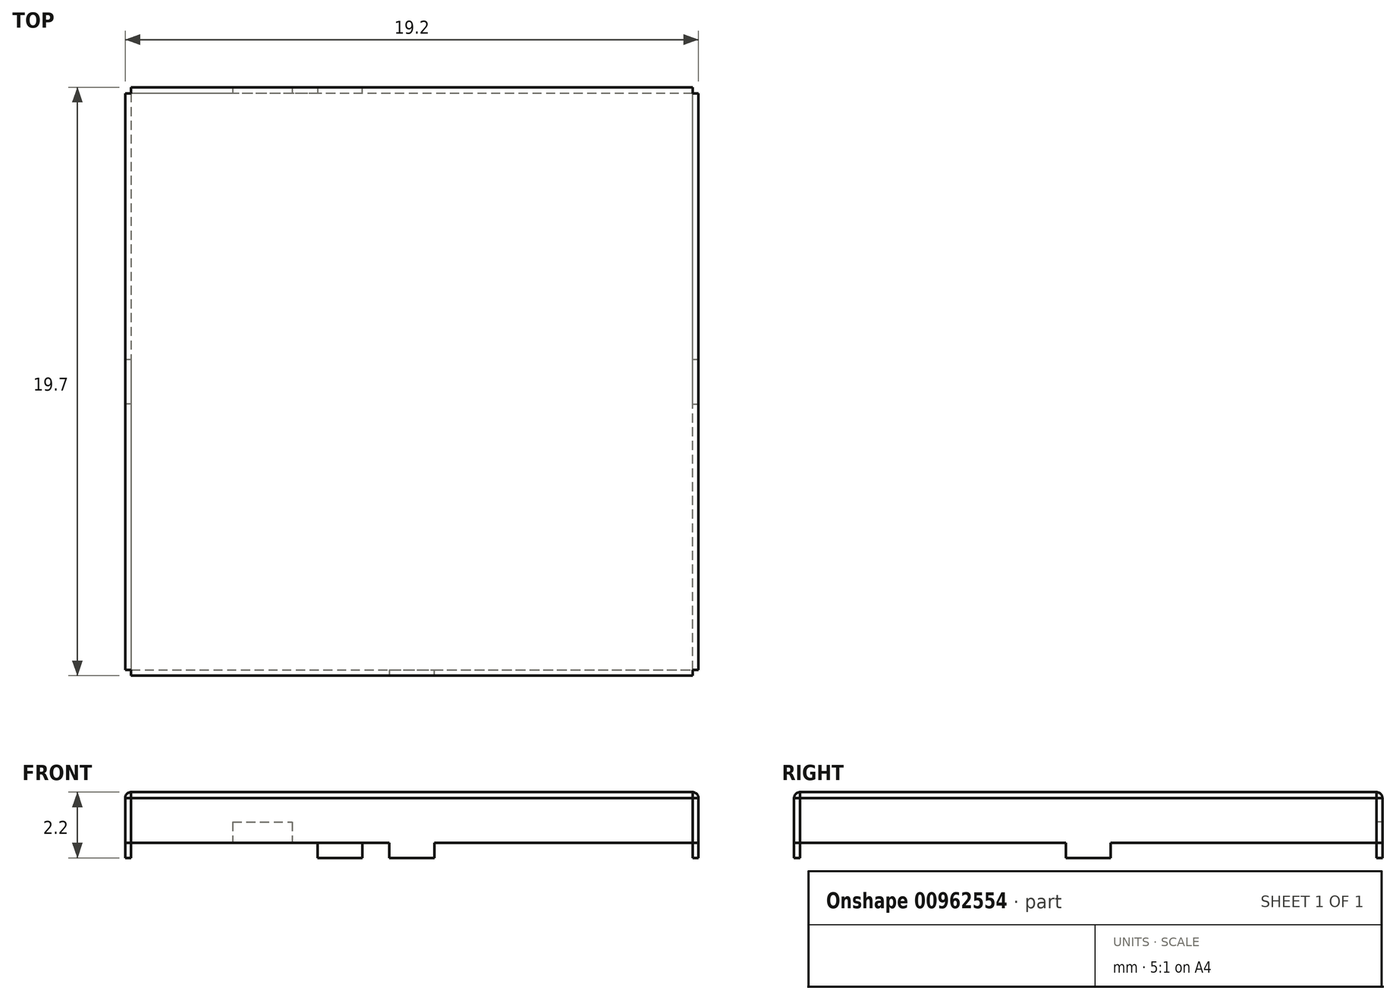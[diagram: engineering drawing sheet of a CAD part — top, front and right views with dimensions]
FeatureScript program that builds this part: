
annotation { "Feature Type Name" : "Feature", "Feature Type Description" : "" }
export const myFeature = defineFeature(function(context is Context, id is Id, definition is map)
    precondition{}
    {
        {
            var Q0;
            Q0=qCreatedBy(makeId("Top.planeOp"),FACE);
            var sketch = newSketch(context, id + "F0", { "sketchPlane" : qUnion([Q0])});
            skLineSegment(sketch, "E0", {"start": v(9.6, 9.65) * mm, "end": v(9.4, 9.65) * mm});
            skLineSegment(sketch, "E1", {"start": v(9.4, 9.65) * mm, "end": v(9.4, 9.85) * mm});
            skLineSegment(sketch, "E2", {"start": v(-9.6, 9.65) * mm, "end": v(-9.4, 9.65) * mm});
            skLineSegment(sketch, "E3", {"start": v(-9.4, 9.65) * mm, "end": v(-9.4, 9.85) * mm});
            skLineSegment(sketch, "E4", {"start": v(9.6, -9.65) * mm, "end": v(9.4, -9.65) * mm});
            skLineSegment(sketch, "E5", {"start": v(9.4, -9.65) * mm, "end": v(9.4, -9.85) * mm});
            skLineSegment(sketch, "E6", {"start": v(-9.6, -9.65) * mm, "end": v(-9.4, -9.65) * mm});
            skLineSegment(sketch, "E7", {"start": v(-9.4, -9.65) * mm, "end": v(-9.4, -9.85) * mm});
            skLineSegment(sketch, "E8", {"start": v(-9.4, 9.85) * mm, "end": v(9.4, 9.85) * mm});
            skLineSegment(sketch, "E9", {"start": v(9.6, 9.65) * mm, "end": v(9.6, -9.65) * mm});
            skLineSegment(sketch, "E10", {"start": v(-9.6, -9.65) * mm, "end": v(-9.6, 9.65) * mm});
            skLineSegment(sketch, "E11", {"start": v(9.4, -9.85) * mm, "end": v(-9.4, -9.85) * mm});
            skLineSegment(sketch, "E12", {"start": v(-9.4, 9.65) * mm, "end": v(-9.4, -9.65) * mm});
            skLineSegment(sketch, "E13", {"start": v(-9.4, -9.65) * mm, "end": v(9.4, -9.65) * mm});
            skLineSegment(sketch, "E14", {"start": v(9.4, -9.65) * mm, "end": v(9.4, 9.65) * mm});
            skLineSegment(sketch, "E15", {"start": v(9.4, 9.65) * mm, "end": v(-9.4, 9.65) * mm});
            skLineSegment(sketch, "E16", {"start": v(-3.15, 9.85) * mm, "end": v(-3.15, 9.65) * mm});
            skLineSegment(sketch, "E17", {"start": v(-1.65, 9.65) * mm, "end": v(-1.65, 9.85) * mm});
            skLineSegment(sketch, "E18", {"start": v(-0.75, -9.65) * mm, "end": v(-0.75, -9.85) * mm});
            skLineSegment(sketch, "E19", {"start": v(0.75, -9.85) * mm, "end": v(0.75, -9.65) * mm});
            skLineSegment(sketch, "E20", {"start": v(-9.6, 0.75) * mm, "end": v(-9.4, 0.75) * mm});
            skLineSegment(sketch, "E21", {"start": v(-9.4, -0.75) * mm, "end": v(-9.6, -0.75) * mm});
            skLineSegment(sketch, "E22", {"start": v(9.4, -0.75) * mm, "end": v(9.6, -0.75) * mm});
            skLineSegment(sketch, "E23", {"start": v(9.4, 0.75) * mm, "end": v(9.6, 0.75) * mm});
            skLineSegment(sketch, "E24", {"start": v(-6, 9.85) * mm, "end": v(-6, 9.65) * mm});
            skLineSegment(sketch, "E25", {"start": v(-4, 9.85) * mm, "end": v(-4, 9.65) * mm});
            skSolve(sketch);
        }
        {
            var Q0;
            {var subQ0=sQuery(id+"F0.wireOp",EDGE,"E3");Q0=makeQuery(id+"F0.imprint","IMPRINT",FACE,{"disambiguationData":[TD([[makeQuery(id+"F0.imprint","IMPRINT",EDGE,{"derivedFrom":subQ0}),-1.0]])]});}
            var Q1;
            {var subQ0=sQuery(id+"F0.wireOp",EDGE,"E24");Q1=makeQuery(id+"F0.imprint","IMPRINT",FACE,{"disambiguationData":[TD([[makeQuery(id+"F0.imprint","IMPRINT",EDGE,{"derivedFrom":subQ0}),1.0]])]});}
            var Q2;
            {var subQ0=sQuery(id+"F0.wireOp",EDGE,"E16");Q2=makeQuery(id+"F0.imprint","IMPRINT",FACE,{"disambiguationData":[TD([[makeQuery(id+"F0.imprint","IMPRINT",EDGE,{"derivedFrom":subQ0}),-1.0]])]});}
            var Q3;
            {var subQ0=sQuery(id+"F0.wireOp",EDGE,"E16");Q3=makeQuery(id+"F0.imprint","IMPRINT",FACE,{"disambiguationData":[TD([[makeQuery(id+"F0.imprint","IMPRINT",EDGE,{"derivedFrom":subQ0}),1.0]])]});}
            var Q4;
            {var subQ0=sQuery(id+"F0.wireOp",EDGE,"E1");Q4=makeQuery(id+"F0.imprint","IMPRINT",FACE,{"disambiguationData":[TD([[makeQuery(id+"F0.imprint","IMPRINT",EDGE,{"derivedFrom":subQ0}),1.0]])]});}
            extrude(context, id + "F1", {"entities" : qUnion([Q0, Q1, Q2, Q3, Q4]), "depth" : 1.5 * mm, "offsetDistance" : 25 * mm});
        }
        {
            var Q0;
            {var subQ0=sQuery(id+"F0.wireOp",EDGE,"E0");Q0=makeQuery(id+"F0.imprint","IMPRINT",FACE,{"disambiguationData":[TD([[makeQuery(id+"F0.imprint","IMPRINT",EDGE,{"derivedFrom":subQ0}),1.0]])]});}
            var Q1;
            {var subQ0=sQuery(id+"F0.wireOp",EDGE,"E22");Q1=makeQuery(id+"F0.imprint","IMPRINT",FACE,{"disambiguationData":[TD([[makeQuery(id+"F0.imprint","IMPRINT",EDGE,{"derivedFrom":subQ0}),1.0]])]});}
            var Q2;
            {var subQ0=sQuery(id+"F0.wireOp",EDGE,"E4");Q2=makeQuery(id+"F0.imprint","IMPRINT",FACE,{"disambiguationData":[TD([[makeQuery(id+"F0.imprint","IMPRINT",EDGE,{"derivedFrom":subQ0}),-1.0]])]});}
            extrude(context, id + "F2", {"entities" : qUnion([Q0, Q1, Q2]), "depth" : 1.5 * mm, "offsetDistance" : 25 * mm});
        }
        {
            var Q0;
            {var subQ0=sQuery(id+"F0.wireOp",EDGE,"E2");Q0=makeQuery(id+"F0.imprint","IMPRINT",FACE,{"disambiguationData":[TD([[makeQuery(id+"F0.imprint","IMPRINT",EDGE,{"derivedFrom":subQ0}),-1.0]])]});}
            var Q1;
            {var subQ0=sQuery(id+"F0.wireOp",EDGE,"E20");Q1=makeQuery(id+"F0.imprint","IMPRINT",FACE,{"disambiguationData":[TD([[makeQuery(id+"F0.imprint","IMPRINT",EDGE,{"derivedFrom":subQ0}),-1.0]])]});}
            var Q2;
            {var subQ0=sQuery(id+"F0.wireOp",EDGE,"E6");Q2=makeQuery(id+"F0.imprint","IMPRINT",FACE,{"disambiguationData":[TD([[makeQuery(id+"F0.imprint","IMPRINT",EDGE,{"derivedFrom":subQ0}),1.0]])]});}
            extrude(context, id + "F3", {"entities" : qUnion([Q0, Q1, Q2]), "depth" : 1.5 * mm, "offsetDistance" : 25 * mm});
        }
        {
            var Q0;
            {var subQ0=sQuery(id+"F0.wireOp",EDGE,"E18");Q0=makeQuery(id+"F0.imprint","IMPRINT",FACE,{"disambiguationData":[TD([[makeQuery(id+"F0.imprint","IMPRINT",EDGE,{"derivedFrom":subQ0}),1.0]])]});}
            var Q1;
            {var subQ0=sQuery(id+"F0.wireOp",EDGE,"E5");Q1=makeQuery(id+"F0.imprint","IMPRINT",FACE,{"disambiguationData":[TD([[makeQuery(id+"F0.imprint","IMPRINT",EDGE,{"derivedFrom":subQ0}),-1.0]])]});}
            var Q2;
            {var subQ0=sQuery(id+"F0.wireOp",EDGE,"E7");Q2=makeQuery(id+"F0.imprint","IMPRINT",FACE,{"disambiguationData":[TD([[makeQuery(id+"F0.imprint","IMPRINT",EDGE,{"derivedFrom":subQ0}),1.0]])]});}
            extrude(context, id + "F4", {"entities" : qUnion([Q0, Q1, Q2]), "depth" : 1.5 * mm, "offsetDistance" : 25 * mm});
        }
        {
            var Q0;
            {var subQ0=sQuery(id+"F0.wireOp",EDGE,"E3");Q0=makeQuery(id+"F0.imprint","IMPRINT",FACE,{"disambiguationData":[TD([[makeQuery(id+"F0.imprint","IMPRINT",EDGE,{"derivedFrom":subQ0}),-1.0]])]});}
            var Q1;
            {var subQ0=sQuery(id+"F0.wireOp",EDGE,"E24");Q1=makeQuery(id+"F0.imprint","IMPRINT",FACE,{"disambiguationData":[TD([[makeQuery(id+"F0.imprint","IMPRINT",EDGE,{"derivedFrom":subQ0}),1.0]])]});}
            var Q2;
            {var subQ0=sQuery(id+"F0.wireOp",EDGE,"E16");Q2=makeQuery(id+"F0.imprint","IMPRINT",FACE,{"disambiguationData":[TD([[makeQuery(id+"F0.imprint","IMPRINT",EDGE,{"derivedFrom":subQ0}),-1.0]])]});}
            var Q3;
            {var subQ0=sQuery(id+"F0.wireOp",EDGE,"E16");Q3=makeQuery(id+"F0.imprint","IMPRINT",FACE,{"disambiguationData":[TD([[makeQuery(id+"F0.imprint","IMPRINT",EDGE,{"derivedFrom":subQ0}),1.0]])]});}
            var Q4;
            {var subQ0=sQuery(id+"F0.wireOp",EDGE,"E1");Q4=makeQuery(id+"F0.imprint","IMPRINT",FACE,{"disambiguationData":[TD([[makeQuery(id+"F0.imprint","IMPRINT",EDGE,{"derivedFrom":subQ0}),1.0]])]});}
            var Q5;
            {var subQ0=sQuery(id+"F0.wireOp",EDGE,"E0");Q5=makeQuery(id+"F0.imprint","IMPRINT",FACE,{"disambiguationData":[TD([[makeQuery(id+"F0.imprint","IMPRINT",EDGE,{"derivedFrom":subQ0}),1.0]])]});}
            var Q6;
            {var subQ10=sQuery(id+"F0.wireOp",EDGE,"E12");var subQ12=makeQuery(id+"F0.imprint","INTERSECT",VERTEX,{"derivedFrom":[subQ10,sQuery(id+"F0.wireOp",EDGE,"E20")]});Q6=makeQuery(id+"F0.imprint","IMPRINT",FACE,{"disambiguationData":[TD([[makeQuery(id+"F0.imprint","IMPRINT",EDGE,{"disambiguationData":[TD([[subQ12,-1.0]])],"derivedFrom":subQ10}),1.0]])]});}
            var Q7;
            {var subQ0=sQuery(id+"F0.wireOp",EDGE,"E2");Q7=makeQuery(id+"F0.imprint","IMPRINT",FACE,{"disambiguationData":[TD([[makeQuery(id+"F0.imprint","IMPRINT",EDGE,{"derivedFrom":subQ0}),-1.0]])]});}
            var Q8;
            {var subQ0=sQuery(id+"F0.wireOp",EDGE,"E20");Q8=makeQuery(id+"F0.imprint","IMPRINT",FACE,{"disambiguationData":[TD([[makeQuery(id+"F0.imprint","IMPRINT",EDGE,{"derivedFrom":subQ0}),-1.0]])]});}
            var Q9;
            {var subQ0=sQuery(id+"F0.wireOp",EDGE,"E6");Q9=makeQuery(id+"F0.imprint","IMPRINT",FACE,{"disambiguationData":[TD([[makeQuery(id+"F0.imprint","IMPRINT",EDGE,{"derivedFrom":subQ0}),1.0]])]});}
            var Q10;
            {var subQ0=sQuery(id+"F0.wireOp",EDGE,"E7");Q10=makeQuery(id+"F0.imprint","IMPRINT",FACE,{"disambiguationData":[TD([[makeQuery(id+"F0.imprint","IMPRINT",EDGE,{"derivedFrom":subQ0}),1.0]])]});}
            var Q11;
            {var subQ0=sQuery(id+"F0.wireOp",EDGE,"E18");Q11=makeQuery(id+"F0.imprint","IMPRINT",FACE,{"disambiguationData":[TD([[makeQuery(id+"F0.imprint","IMPRINT",EDGE,{"derivedFrom":subQ0}),1.0]])]});}
            var Q12;
            {var subQ0=sQuery(id+"F0.wireOp",EDGE,"E5");Q12=makeQuery(id+"F0.imprint","IMPRINT",FACE,{"disambiguationData":[TD([[makeQuery(id+"F0.imprint","IMPRINT",EDGE,{"derivedFrom":subQ0}),-1.0]])]});}
            var Q13;
            {var subQ0=sQuery(id+"F0.wireOp",EDGE,"E4");Q13=makeQuery(id+"F0.imprint","IMPRINT",FACE,{"disambiguationData":[TD([[makeQuery(id+"F0.imprint","IMPRINT",EDGE,{"derivedFrom":subQ0}),-1.0]])]});}
            var Q14;
            {var subQ0=sQuery(id+"F0.wireOp",EDGE,"E22");Q14=makeQuery(id+"F0.imprint","IMPRINT",FACE,{"disambiguationData":[TD([[makeQuery(id+"F0.imprint","IMPRINT",EDGE,{"derivedFrom":subQ0}),1.0]])]});}
            extrude(context, id + "F5", {"entities" : qUnion([Q0, Q1, Q2, Q3, Q4, Q5, Q6, Q7, Q8, Q9, Q10, Q11, Q12, Q13, Q14]), "depth" : 1.7 * mm, "offsetDistance" : 25 * mm, "hasSecondDirection" : true, "secondDirectionOppositeDirection" : false, "secondDirectionDepth" : 1.5 * mm});
        }
        {
            var Q0;
            {var subQ0=sQuery(id+"F0.wireOp",EDGE,"E24");Q0=makeQuery(id+"F0.imprint","IMPRINT",FACE,{"disambiguationData":[TD([[makeQuery(id+"F0.imprint","IMPRINT",EDGE,{"derivedFrom":subQ0}),1.0]])]});}
            extrude(context, id + "F6", {"entities" : qUnion([Q0]), "operationType" : NewBodyOperationType.REMOVE, "depth" : 0.7 * mm, "offsetDistance" : 25 * mm});
        }
        {
            var Q0;
            {var subQ0=sQuery(id+"F0.wireOp",EDGE,"E16");Q0=makeQuery(id+"F0.imprint","IMPRINT",FACE,{"disambiguationData":[TD([[makeQuery(id+"F0.imprint","IMPRINT",EDGE,{"derivedFrom":subQ0}),1.0]])]});}
            var Q1;
            {var subQ0=sQuery(id+"F0.wireOp",EDGE,"E22");Q1=makeQuery(id+"F0.imprint","IMPRINT",FACE,{"disambiguationData":[TD([[makeQuery(id+"F0.imprint","IMPRINT",EDGE,{"derivedFrom":subQ0}),1.0]])]});}
            var Q2;
            {var subQ0=sQuery(id+"F0.wireOp",EDGE,"E18");Q2=makeQuery(id+"F0.imprint","IMPRINT",FACE,{"disambiguationData":[TD([[makeQuery(id+"F0.imprint","IMPRINT",EDGE,{"derivedFrom":subQ0}),1.0]])]});}
            var Q3;
            {var subQ0=sQuery(id+"F0.wireOp",EDGE,"E20");Q3=makeQuery(id+"F0.imprint","IMPRINT",FACE,{"disambiguationData":[TD([[makeQuery(id+"F0.imprint","IMPRINT",EDGE,{"derivedFrom":subQ0}),-1.0]])]});}
            extrude(context, id + "F7", {"entities" : qUnion([Q0, Q1, Q2, Q3]), "operationType" : NewBodyOperationType.ADD, "oppositeDirection" : true, "depth" : 0.5 * mm, "offsetDistance" : 25 * mm});
        }
        {
            var Q0;
            Q0=makeQuery(id+"F5.opExtrude","CAP_EDGE",EDGE,{"disambiguationData":[OSD([sQuery(id+"F0.wireOp",EDGE,"E10")])],"isStart":false});
            var Q1;
            Q1=makeQuery(id+"F5.opExtrude","CAP_EDGE",EDGE,{"disambiguationData":[OSD([sQuery(id+"F0.wireOp",EDGE,"E8")])],"isStart":false});
            var Q2;
            Q2=makeQuery(id+"F5.opExtrude","CAP_EDGE",EDGE,{"disambiguationData":[OSD([sQuery(id+"F0.wireOp",EDGE,"E9")])],"isStart":false});
            var Q3;
            Q3=makeQuery(id+"F5.opExtrude","CAP_EDGE",EDGE,{"disambiguationData":[OSD([sQuery(id+"F0.wireOp",EDGE,"E11")])],"isStart":false});
            fillet(context, id + "F8", {"entities" : qUnion([Q0, Q1, Q2, Q3]), "radius" : 0.2 * mm, "tangentPropagation" : true, "allowEdgeOverflow" : false});
        }
    });
